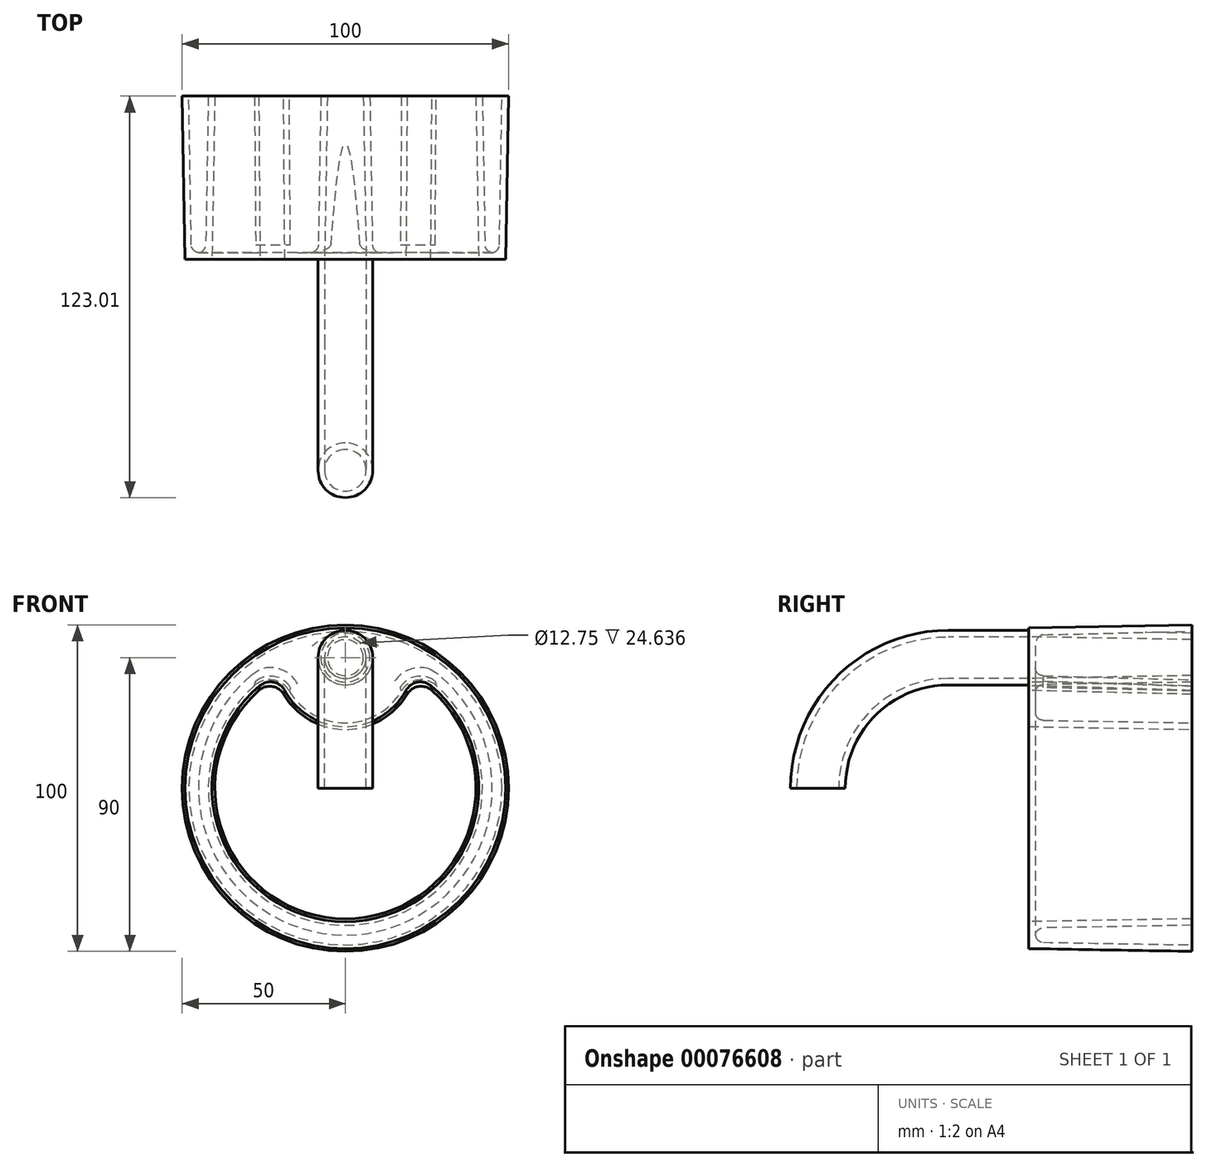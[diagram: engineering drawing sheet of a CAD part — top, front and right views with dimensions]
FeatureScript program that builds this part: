
annotation { "Feature Type Name" : "Feature", "Feature Type Description" : "" }
export const myFeature = defineFeature(function(context is Context, id is Id, definition is map)
    precondition{}
    {
        {
            var Q0;
            Q0=qCreatedBy(makeId("Front.planeOp"),FACE);
            var sketch = newSketch(context, id + "F0", { "sketchPlane" : qUnion([Q0])});
            skCircle(sketch, "E0", {"center": v(0, 0) * mm, "radius": 50 * mm});
            skArc(sketch, "E1", {"start": v(-21.15, 33.95) * mm, "mid": v(0, -40) * mm, "end": v(21.15, 33.95) * mm});
            skArc(sketch, "E2", {"start": v(-21.15, 33.95) * mm, "mid": v(0, 18) * mm, "end": v(21.15, 33.95) * mm});
            skCircle(sketch, "E3", {"center": v(0, 40) * mm, "radius": 5.5 * mm});
            skSolve(sketch);
        }
        {
            var Q0;
            Q0 = qSketchRegion(id + "F0", true);
            extrude(context, id + "F1", {"entities" : qUnion([Q0]), "depth" : 50 * mm, "hasDraft" : true, "draftAngle" : 1 * degree, "draftPullDirection" : true});
        }
        {
            var Q0;
            {var subQ0=sQuery(id+"F0.wireOp",EDGE,"E2");var subQ1=sQuery(id+"F0.wireOp",EDGE,"E1");Q0=makeQuery(id+"F1.opExtrude","SWEPT_EDGE",EDGE,{"disambiguationData":[OSD([subQ1,subQ0]),TDD([makeQuery(id+"F0.imprint","INTERSECT",VERTEX,{"disambiguationData":[OD(0.0)],"derivedFrom":[subQ1,subQ0]})])]});}
            var Q1;
            {var subQ0=sQuery(id+"F0.wireOp",EDGE,"E2");var subQ1=sQuery(id+"F0.wireOp",EDGE,"E1");Q1=makeQuery(id+"F1.opExtrude","SWEPT_EDGE",EDGE,{"disambiguationData":[OSD([subQ1,subQ0]),TDD([makeQuery(id+"F0.imprint","INTERSECT",VERTEX,{"disambiguationData":[OD(1.0)],"derivedFrom":[subQ1,subQ0]})])]});}
            fillet(context, id + "F2", {"entities" : qUnion([Q0, Q1]), "radius" : 5 * mm, "tangentPropagation" : true, "allowEdgeOverflow" : false});
        }
        {
            var Q0;
            Q0=makeQuery(id+"F1.opExtrude","CAP_FACE",FACE,{"disambiguationData":[OSD([sQuery(id+"F0.wireOp",EDGE,"E0"),sQuery(id+"F0.wireOp",EDGE,"E1"),sQuery(id+"F0.wireOp",EDGE,"E2"),sQuery(id+"F0.wireOp",EDGE,"E3")])],"isStart":true});
            shell(context, id + "F3", {"entities" : qUnion([Q0]), "thickness" : 2 * mm});
        }
        {
            var Q0;
            {var subQ0=sQuery(id+"F0.wireOp",EDGE,"E2");Q0=makeQuery(id+"F3.opShell","OFFSET_EDGE",EDGE,{"disambiguationData":[OSD([subQ0]),TDD([makeQuery(id+"F1.opExtrude","CAP_EDGE",EDGE,{"disambiguationData":[OSD([subQ0])],"isStart":false})])]});}
            var Q1;
            {var subQ0=sQuery(id+"F0.wireOp",EDGE,"E0");Q1=makeQuery(id+"F3.opShell","OFFSET_EDGE",EDGE,{"disambiguationData":[OSD([subQ0]),TDD([makeQuery(id+"F1.opExtrude","CAP_EDGE",EDGE,{"disambiguationData":[OSD([subQ0])],"isStart":false})])]});}
            var Q2;
            {var subQ0=sQuery(id+"F0.wireOp",EDGE,"E3");Q2=makeQuery(id+"F3.opShell","OFFSET_EDGE",EDGE,{"disambiguationData":[OSD([subQ0]),TDD([makeQuery(id+"F1.opExtrude","CAP_EDGE",EDGE,{"disambiguationData":[OSD([subQ0])],"isStart":false})])]});}
            fillet(context, id + "F4", {"entities" : qUnion([Q0, Q1, Q2]), "radius" : 2.5 * mm, "tangentPropagation" : true, "allowEdgeOverflow" : false});
        }
        {
            var Q0;
            Q0=makeQuery(id+"F1.opExtrude","CAP_FACE",FACE,{"disambiguationData":[OSD([sQuery(id+"F0.wireOp",EDGE,"E0"),sQuery(id+"F0.wireOp",EDGE,"E1"),sQuery(id+"F0.wireOp",EDGE,"E2"),sQuery(id+"F0.wireOp",EDGE,"E3")])],"isStart":false});
            var sketch = newSketch(context, id + "F5", { "sketchPlane" : qUnion([Q0])});
            skCircle(sketch, "E4.0", {"center": v(0, 40) * mm, "radius": 6.37 * mm});
            skCircle(sketch, "E5.0", {"center": v(0, 40) * mm, "radius": 8.37 * mm});
            skSolve(sketch);
        }
        {
            var Q0;
            Q0=qCreatedBy(makeId("Right.planeOp"),FACE);
            var sketch = newSketch(context, id + "F6", { "sketchPlane" : qUnion([Q0])});
            skLineSegment(sketch, "E6", {"start": v(-50, 40) * mm, "end": v(-74.64, 40) * mm});
            skArc(sketch, "E7", {"start": v(-74.64, 40) * mm, "mid": v(-102.92, 28.28) * mm, "end": v(-114.64, 0) * mm});
            skSolve(sketch);
        }
        {
            var Q0;
            Q0 = qSketchRegion(id + "F5", true);
            var Q1;
            Q1=sQuery(id+"F6.wireOp",EDGE,"E6");
            var Q2;
            Q2=sQuery(id+"F6.wireOp",EDGE,"E7");
            sweep(context, id + "F7", {"profiles" : qUnion([Q0]), "path" : qUnion([Q1, Q2])});
        }
    });
